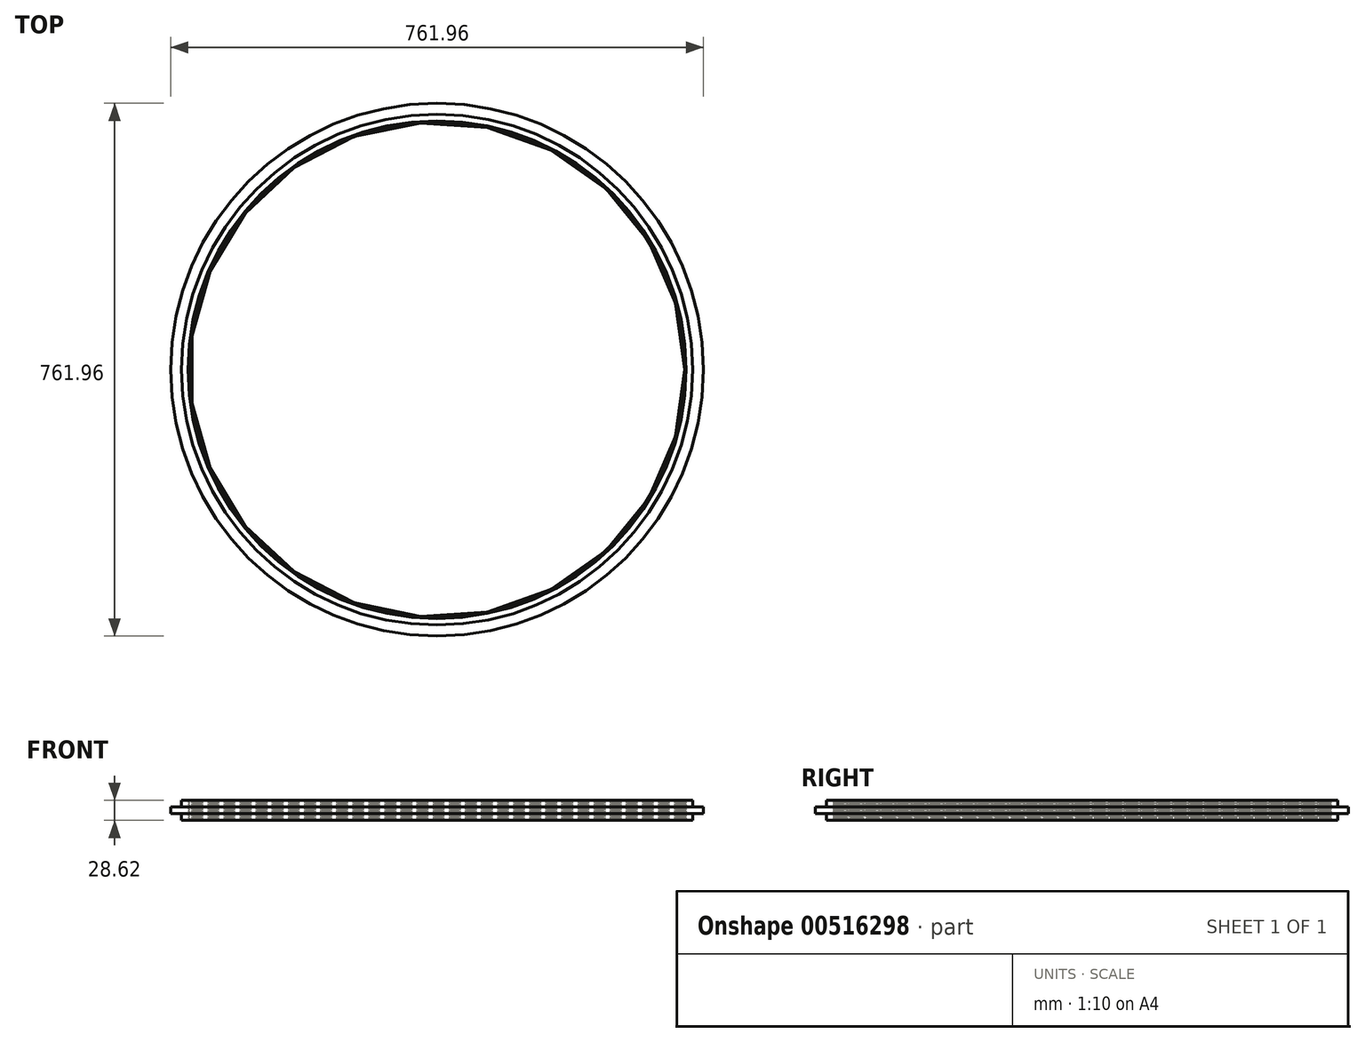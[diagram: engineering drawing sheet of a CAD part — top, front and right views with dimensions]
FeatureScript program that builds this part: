
annotation { "Feature Type Name" : "Feature", "Feature Type Description" : "" }
export const myFeature = defineFeature(function(context is Context, id is Id, definition is map)
    precondition{}
    {
        {
            var Q0;
            Q0=qCreatedBy(makeId("Front.planeOp"),FACE);
            var sketch = newSketch(context, id + "F0", { "sketchPlane" : qUnion([Q0])});
            skLineSegment(sketch, "E0", {"start": v(0, 0) * mm, "end": v(0, -186.36) * mm});
            skLineSegment(sketch, "E1.0", {"start": v(380.98, -9.53) * mm, "end": v(380.98, -19.06) * mm});
            skLineSegment(sketch, "E2", {"start": v(365.23, 0.04) * mm, "end": v(365.23, -9.53) * mm});
            skLineSegment(sketch, "E3.0", {"start": v(365.23, -19.06) * mm, "end": v(380.98, -19.06) * mm});
            skLineSegment(sketch, "E4.trimOffspring", {"start": v(365.23, -9.53) * mm, "end": v(380.98, -9.53) * mm});
            skPoint(sketch, "E5", {"position": v(353.78, -25.4) * mm});
            skLineSegment(sketch, "E6.trimOffspring", {"start": v(365.23, -19.06) * mm, "end": v(365.23, -28.58) * mm});
            skLineSegment(sketch, "E7", {"start": v(353.78, -25.4) * mm, "end": v(355.61, -28.58) * mm});
            skPoint(sketch, "E8.orphan", {"position": v(353.78, -28.58) * mm});
            skLineSegment(sketch, "E9", {"start": v(353.78, -25.4) * mm, "end": v(355.7, -25.57) * mm});
            skPoint(sketch, "E10", {"position": v(353.78, -22.22) * mm});
            skLineSegment(sketch, "E11", {"start": v(353.78, -22.22) * mm, "end": v(355.7, -25.57) * mm});
            skLineSegment(sketch, "E12.1.0.0", {"start": v(353.78, -22.22) * mm, "end": v(355.7, -22.39) * mm});
            skPoint(sketch, "E13", {"position": v(353.78, -19.04) * mm});
            skLineSegment(sketch, "E14", {"start": v(353.78, -19.04) * mm, "end": v(355.7, -22.39) * mm});
            skLineSegment(sketch, "E15.1.0.0", {"start": v(353.78, -19.04) * mm, "end": v(355.7, -19.2) * mm});
            skPoint(sketch, "E16", {"position": v(353.78, -15.86) * mm});
            skLineSegment(sketch, "E17", {"start": v(353.78, -15.86) * mm, "end": v(355.7, -19.2) * mm});
            skLineSegment(sketch, "E18.1.0.0", {"start": v(353.78, -15.86) * mm, "end": v(355.7, -16.03) * mm});
            skPoint(sketch, "E19", {"position": v(353.78, -12.68) * mm});
            skLineSegment(sketch, "E20", {"start": v(353.78, -12.68) * mm, "end": v(355.7, -16.03) * mm});
            skLineSegment(sketch, "E21.1.0.0", {"start": v(353.78, -12.68) * mm, "end": v(355.7, -12.85) * mm});
            skPoint(sketch, "E22", {"position": v(353.78, -9.5) * mm});
            skLineSegment(sketch, "E23", {"start": v(353.78, -9.5) * mm, "end": v(355.7, -12.85) * mm});
            skLineSegment(sketch, "E24.1.0.0", {"start": v(353.78, -9.5) * mm, "end": v(355.7, -9.67) * mm});
            skPoint(sketch, "E25", {"position": v(353.78, -6.32) * mm});
            skLineSegment(sketch, "E26", {"start": v(353.78, -6.32) * mm, "end": v(355.7, -9.67) * mm});
            skLineSegment(sketch, "E27.1.0.0", {"start": v(353.78, -6.32) * mm, "end": v(355.7, -6.49) * mm});
            skPoint(sketch, "E28", {"position": v(353.78, -3.14) * mm});
            skLineSegment(sketch, "E29", {"start": v(353.78, -3.14) * mm, "end": v(355.7, -6.49) * mm});
            skLineSegment(sketch, "E30.1.0.0", {"start": v(353.78, -3.14) * mm, "end": v(355.7, -3.3) * mm});
            skPoint(sketch, "E31", {"position": v(353.78, 0.04) * mm});
            skLineSegment(sketch, "E32", {"start": v(353.78, 0.04) * mm, "end": v(355.7, -3.3) * mm});
            skLineSegment(sketch, "E33.1.0.0", {"start": v(353.78, 0.04) * mm, "end": v(355.7, -0.13) * mm});
            skLineSegment(sketch, "E34", {"start": v(355.88, 0.04) * mm, "end": v(365.23, 0.04) * mm});
            skLineSegment(sketch, "E35", {"start": v(355.61, -28.58) * mm, "end": v(365.23, -28.58) * mm});
            skArc(sketch, "E36", {"start": v(355.68, -0.13) * mm, "mid": v(355.82, -0.1) * mm, "end": v(355.88, 0.04) * mm});
            skSolve(sketch);
        }
        {
            var Q0;
            Q0 = qSketchRegion(id + "F0", true);
            var Q1;
            Q1=sQuery(id+"F0.wireOp",EDGE,"E0");
            revolve(context, id + "F1", {"entities" : qUnion([Q0]), "axis" : qUnion([Q1]), "revolveType" : RevolveType.FULL});
        }
    });
